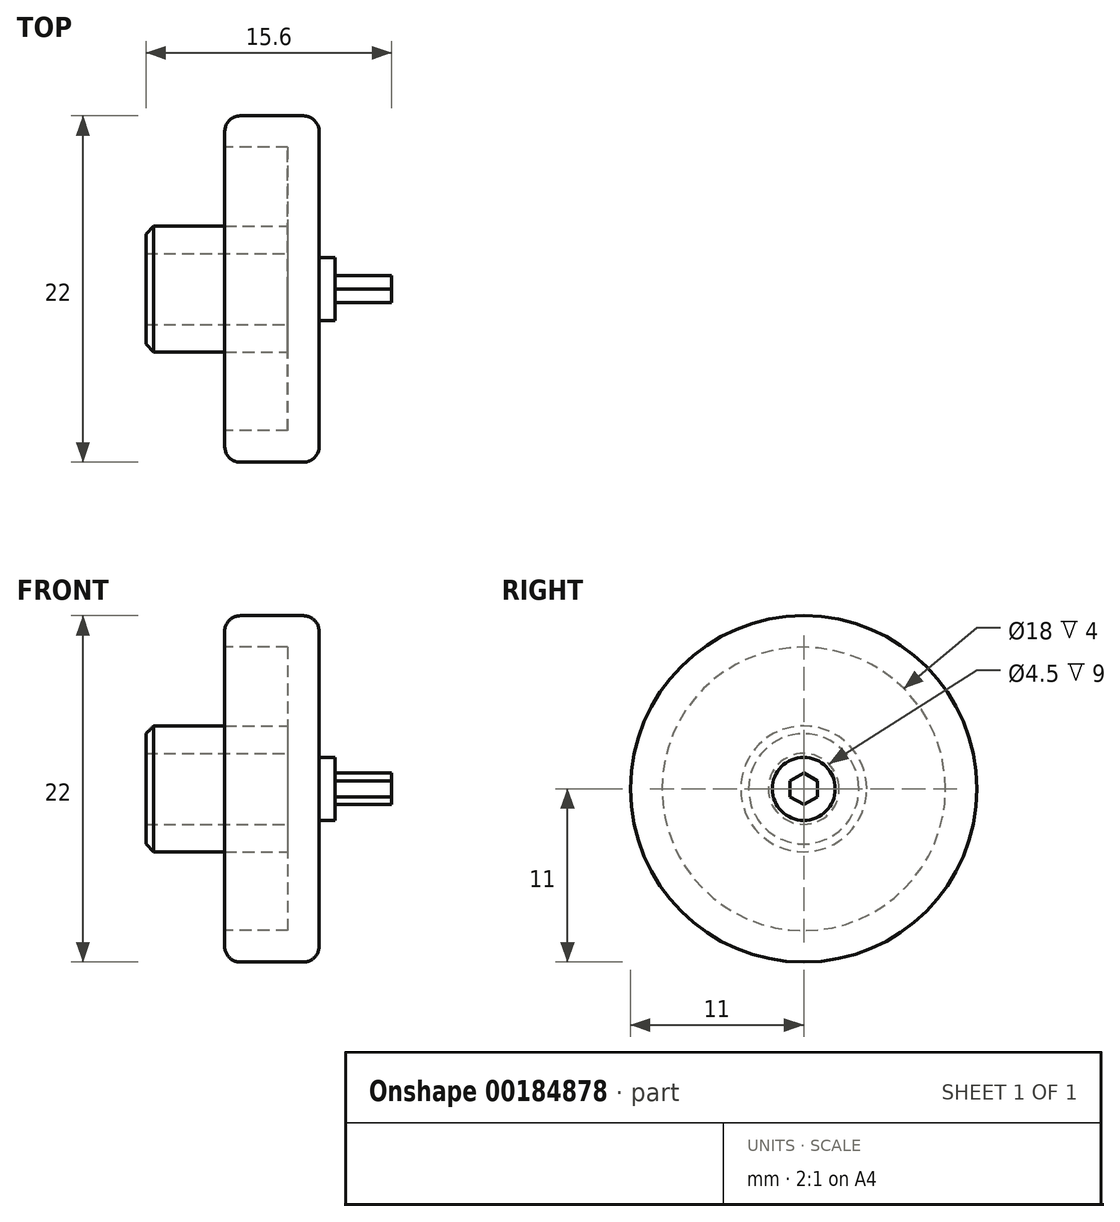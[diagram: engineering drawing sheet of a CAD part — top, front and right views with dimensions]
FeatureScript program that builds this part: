
annotation { "Feature Type Name" : "Feature", "Feature Type Description" : "" }
export const myFeature = defineFeature(function(context is Context, id is Id, definition is map)
    precondition{}
    {
        {
            var Q0;
            Q0=qCreatedBy(makeId("Right.planeOp"),FACE);
            var sketch = newSketch(context, id + "F0", { "sketchPlane" : qUnion([Q0])});
            skCircle(sketch, "E0", {"center": v(0, 0) * mm, "radius": 11 * mm});
            skSolve(sketch);
        }
        {
            var Q0;
            Q0=qSketchRegion(id+"F0",true);
            extrude(context, id + "F1", {"entities" : qUnion([Q0]), "endBound" : BoundingType.SYMMETRIC, "depth" : 6 * mm});
        }
        {
            var Q0;
            Q0=makeQuery(id+"F1.opExtrude","CAP_EDGE",EDGE,{"disambiguationData":[OSD([sQuery(id+"F0.wireOp",EDGE,"E0")])],"isStart":true});
            var Q1;
            Q1=makeQuery(id+"F1.opExtrude","CAP_EDGE",EDGE,{"disambiguationData":[OSD([sQuery(id+"F0.wireOp",EDGE,"E0")])],"isStart":false});
            fillet(context, id + "F2", {"entities" : qUnion([Q0, Q1]), "radius" : 1 * mm, "tangentPropagation" : true, "allowEdgeOverflow" : false});
        }
        {
            var Q0;
            Q0=makeQuery(id+"F1.opExtrude","CAP_FACE",FACE,{"disambiguationData":[OSD([sQuery(id+"F0.wireOp",EDGE,"E0")])],"isStart":true});
            var sketch = newSketch(context, id + "F3", { "sketchPlane" : qUnion([Q0])});
            skCircle(sketch, "E1", {"center": v(0, 0) * mm, "radius": 9 * mm});
            skSolve(sketch);
        }
        {
            var Q0;
            Q0=qSketchRegion(id+"F3",true);
            extrude(context, id + "F4", {"entities" : qUnion([Q0]), "operationType" : NewBodyOperationType.REMOVE, "oppositeDirection" : true, "depth" : 4 * mm});
        }
        {
            var Q0;
            Q0=makeQuery(id+"F4.boolean.opBoolean","COPY",FACE,{"derivedFrom":makeQuery(id+"F4.opExtrude","CAP_FACE",FACE,{"disambiguationData":[OSD([sQuery(id+"F3.wireOp",EDGE,"E1")])],"isStart":false})});
            var sketch = newSketch(context, id + "F5", { "sketchPlane" : qUnion([Q0])});
            skCircle(sketch, "E2", {"center": v(0, 0) * mm, "radius": 4 * mm});
            skCircle(sketch, "E3", {"center": v(0, 0) * mm, "radius": 2.25 * mm});
            skSolve(sketch);
        }
        {
            var Q0;
            Q0=qSketchRegion(id+"F5",true);
            extrude(context, id + "F6", {"entities" : qUnion([Q0]), "operationType" : NewBodyOperationType.ADD, "depth" : 9 * mm});
        }
        {
            var Q0;
            Q0=makeQuery(id+"F1.opExtrude","CAP_FACE",FACE,{"disambiguationData":[OSD([sQuery(id+"F0.wireOp",EDGE,"E0")])],"isStart":false});
            var sketch = newSketch(context, id + "F7", { "sketchPlane" : qUnion([Q0])});
            skCircle(sketch, "E4", {"center": v(0, 0) * mm, "radius": 2 * mm});
            skSolve(sketch);
        }
        {
            var Q0;
            Q0=qSketchRegion(id+"F7",true);
            extrude(context, id + "F8", {"entities" : qUnion([Q0]), "operationType" : NewBodyOperationType.ADD, "depth" : 1 * mm});
        }
        {
            var Q0;
            Q0=makeQuery(id+"F8.opExtrude","CAP_FACE",FACE,{"disambiguationData":[OSD([sQuery(id+"F7.wireOp",EDGE,"E4")])],"isStart":false});
            var sketch = newSketch(context, id + "F9", { "sketchPlane" : qUnion([Q0])});
            skCircle(sketch, "E5.cCircle", {"center": v(0, 0) * mm, "radius": 1 * mm, "construction": true});
            skLineSegment(sketch, "E5.0", {"start": v(0.86, 0.5) * mm, "end": v(0.87, -0.5) * mm});
            skLineSegment(sketch, "E5.1", {"start": v(0.86, -0.5) * mm, "end": v(0, -1) * mm});
            skLineSegment(sketch, "E5.2", {"start": v(0, -1) * mm, "end": v(-0.86, -0.5) * mm});
            skLineSegment(sketch, "E5.3", {"start": v(-0.86, -0.5) * mm, "end": v(-0.87, 0.5) * mm});
            skLineSegment(sketch, "E5.4", {"start": v(-0.87, 0.5) * mm, "end": v(0, 1) * mm});
            skLineSegment(sketch, "E5.5", {"start": v(0, 1) * mm, "end": v(0.86, 0.5) * mm});
            skLineSegment(sketch, "E6", {"start": v(0, 0.15) * mm, "end": v(0, 0.7) * mm, "construction": true});
            skSolve(sketch);
        }
        {
            var Q0;
            Q0=qSketchRegion(id+"F9",true);
            extrude(context, id + "F10", {"entities" : qUnion([Q0]), "operationType" : NewBodyOperationType.ADD, "depth" : 3.6 * mm});
        }
        {
            var Q0;
            Q0=makeQuery(id+"F6.opExtrude","CAP_EDGE",EDGE,{"disambiguationData":[OSD([sQuery(id+"F5.wireOp",EDGE,"E2")])],"isStart":false});
            chamfer(context, id + "F11", {"entities" : qUnion([Q0]), "width" : 0.5 * mm, "tangentPropagation" : true});
        }
    });
